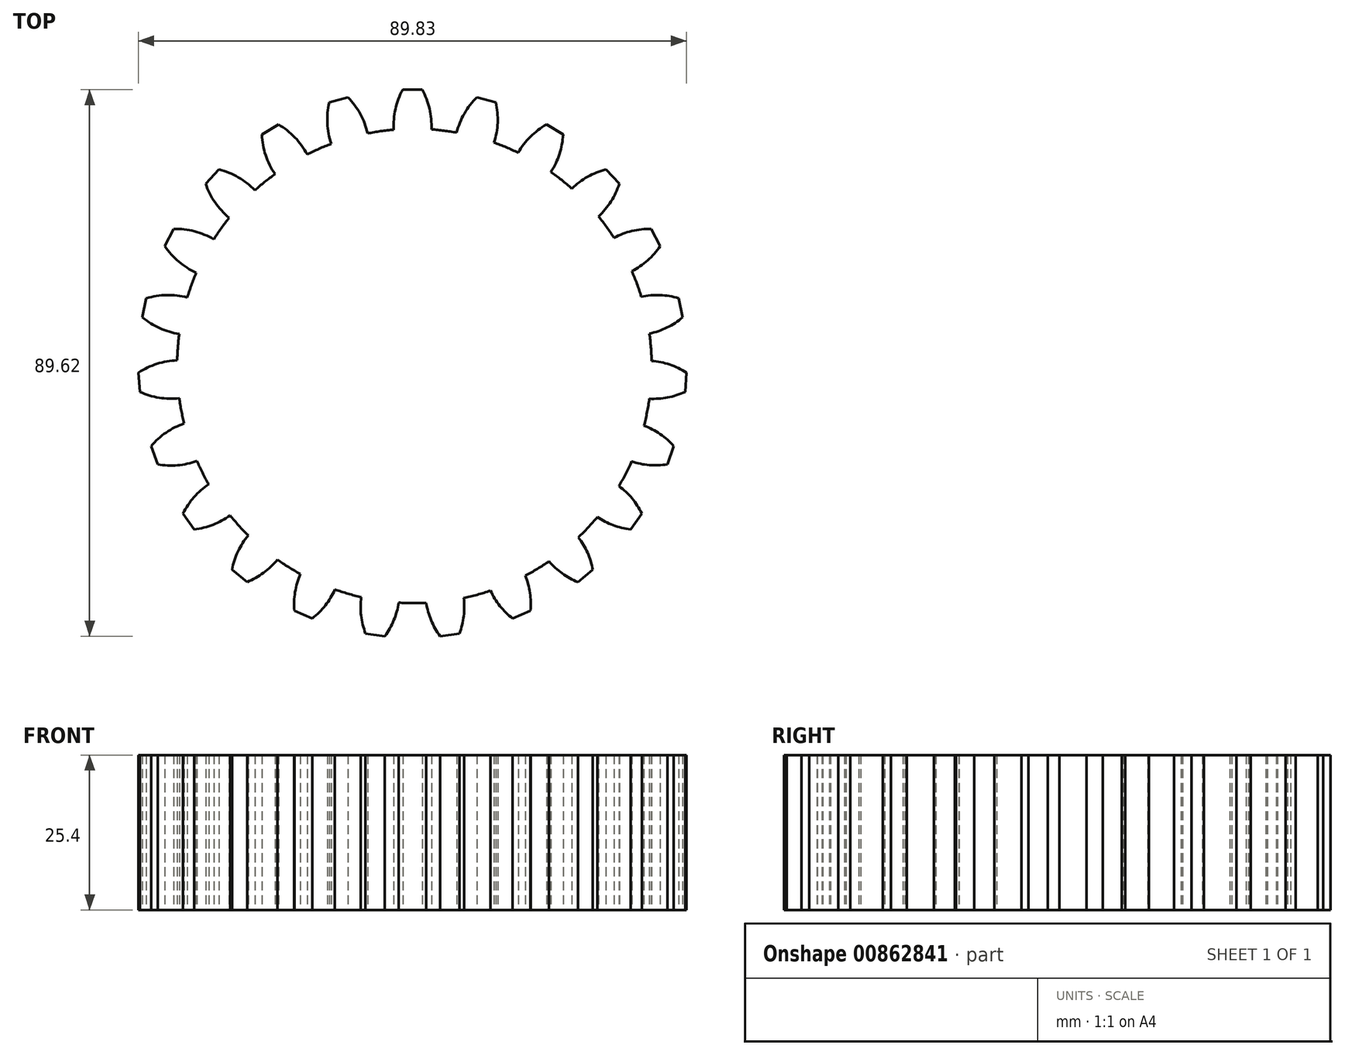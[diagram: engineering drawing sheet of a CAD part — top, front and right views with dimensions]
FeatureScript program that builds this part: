
annotation { "Feature Type Name" : "Feature", "Feature Type Description" : "" }
export const myFeature = defineFeature(function(context is Context, id is Id, definition is map)
    precondition{}
    {
        {
            var Q0;
            Q0=qCreatedBy(makeId("Top.planeOp"),FACE);
            var sketch = newSketch(context, id + "F0", { "sketchPlane" : qUnion([Q0])});
            skLineSegment(sketch, "E0.22.2", {"start": v(40.96, 115) * mm, "end": v(42.5, 115.43) * mm});
            skCircle(sketch, "E1", {"center": v(0, 0) * mm, "radius": 38.9 * mm});
            skArc(sketch, "E2", {"start": v(-1.9, 45.32) * mm, "mid": v(-3.1, 42.14) * mm, "end": v(-3.38, 38.75) * mm});
            skLineSegment(sketch, "E3", {"start": v(-1.9, 45.32) * mm, "end": v(-0.31, 45.32) * mm});
            skArc(sketch, "E4.MirrorCS", {"start": v(1.28, 45.32) * mm, "mid": v(2.49, 42.17) * mm, "end": v(2.8, 38.8) * mm});
            skLineSegment(sketch, "E5.MirrorCS", {"start": v(1.28, 45.32) * mm, "end": v(-0.31, 45.32) * mm});
            skArc(sketch, "E6.1.0", {"start": v(10.27, 44.08) * mm, "mid": v(8.2, 41.41) * mm, "end": v(6.92, 38.28) * mm});
            skArc(sketch, "E6.1.1", {"start": v(13.34, 43.23) * mm, "mid": v(13.65, 39.91) * mm, "end": v(13.07, 36.64) * mm});
            skLineSegment(sketch, "E6.1.2", {"start": v(10.27, 44.08) * mm, "end": v(11.8, 43.65) * mm});
            skLineSegment(sketch, "E6.1.3", {"start": v(13.34, 43.23) * mm, "end": v(11.8, 43.65) * mm});
            skArc(sketch, "E6.2.0", {"start": v(21.66, 39.6) * mm, "mid": v(19.03, 37.6) * mm, "end": v(17.02, 34.98) * mm});
            skArc(sketch, "E6.2.1", {"start": v(24.38, 37.96) * mm, "mid": v(23.79, 34.76) * mm, "end": v(22.37, 31.82) * mm});
            skLineSegment(sketch, "E6.2.2", {"start": v(21.66, 39.6) * mm, "end": v(23.02, 38.78) * mm});
            skLineSegment(sketch, "E6.2.3", {"start": v(24.38, 37.96) * mm, "end": v(23.02, 38.78) * mm});
            skArc(sketch, "E6.3.0", {"start": v(31.42, 32.23) * mm, "mid": v(28.41, 31.04) * mm, "end": v(25.81, 29.1) * mm});
            skArc(sketch, "E6.3.1", {"start": v(33.6, 29.9) * mm, "mid": v(32.25, 27) * mm, "end": v(30.2, 24.53) * mm});
            skLineSegment(sketch, "E6.3.2", {"start": v(31.42, 32.23) * mm, "end": v(32.5, 31.06) * mm});
            skLineSegment(sketch, "E6.3.3", {"start": v(33.6, 29.9) * mm, "end": v(32.5, 31.06) * mm});
            skArc(sketch, "E6.4.0", {"start": v(38.83, 22.48) * mm, "mid": v(35.67, 22.15) * mm, "end": v(32.7, 21.01) * mm});
            skArc(sketch, "E6.4.1", {"start": v(40.3, 19.66) * mm, "mid": v(38.2, 17.27) * mm, "end": v(35.56, 15.5) * mm});
            skLineSegment(sketch, "E6.4.2", {"start": v(38.83, 22.48) * mm, "end": v(39.56, 21.07) * mm});
            skLineSegment(sketch, "E6.4.3", {"start": v(40.3, 19.66) * mm, "end": v(39.56, 21.07) * mm});
            skArc(sketch, "E6.5.0", {"start": v(43.33, 11.1) * mm, "mid": v(40.2, 11.63) * mm, "end": v(37.04, 11.34) * mm});
            skArc(sketch, "E6.5.1", {"start": v(43.98, 7.99) * mm, "mid": v(41.32, 6.26) * mm, "end": v(38.3, 5.26) * mm});
            skLineSegment(sketch, "E6.5.2", {"start": v(43.33, 11.1) * mm, "end": v(43.66, 9.55) * mm});
            skLineSegment(sketch, "E6.5.3", {"start": v(43.98, 7.99) * mm, "end": v(43.66, 9.55) * mm});
            skArc(sketch, "E6.6.0", {"start": v(44.6, -1.07) * mm, "mid": v(41.73, 0.28) * mm, "end": v(38.6, 0.86) * mm});
            skArc(sketch, "E6.6.1", {"start": v(44.38, -4.24) * mm, "mid": v(41.35, -5.2) * mm, "end": v(38.18, -5.34) * mm});
            skLineSegment(sketch, "E6.6.2", {"start": v(44.6, -1.07) * mm, "end": v(44.5, -2.66) * mm});
            skLineSegment(sketch, "E6.6.3", {"start": v(44.38, -4.24) * mm, "end": v(44.5, -2.66) * mm});
            skArc(sketch, "E6.7.0", {"start": v(42.54, -13.13) * mm, "mid": v(40.13, -11.05) * mm, "end": v(37.28, -9.66) * mm});
            skArc(sketch, "E6.7.1", {"start": v(41.47, -16.13) * mm, "mid": v(38.3, -16.23) * mm, "end": v(35.2, -15.5) * mm});
            skLineSegment(sketch, "E6.7.2", {"start": v(42.54, -13.13) * mm, "end": v(42, -14.63) * mm});
            skLineSegment(sketch, "E6.7.3", {"start": v(41.47, -16.13) * mm, "end": v(42, -14.63) * mm});
            skArc(sketch, "E6.8.0", {"start": v(37.3, -24.19) * mm, "mid": v(35.54, -21.54) * mm, "end": v(33.17, -19.43) * mm});
            skArc(sketch, "E6.8.1", {"start": v(35.46, -26.8) * mm, "mid": v(32.38, -26.03) * mm, "end": v(29.59, -24.5) * mm});
            skLineSegment(sketch, "E6.8.2", {"start": v(37.3, -24.19) * mm, "end": v(36.38, -25.49) * mm});
            skLineSegment(sketch, "E6.8.3", {"start": v(35.46, -26.8) * mm, "end": v(36.38, -25.49) * mm});
            skArc(sketch, "E6.9.0", {"start": v(29.26, -33.42) * mm, "mid": v(28.29, -30.4) * mm, "end": v(26.58, -27.72) * mm});
            skArc(sketch, "E6.9.1", {"start": v(26.8, -35.43) * mm, "mid": v(24.03, -33.86) * mm, "end": v(21.76, -31.64) * mm});
            skLineSegment(sketch, "E6.9.2", {"start": v(29.26, -33.42) * mm, "end": v(28.03, -34.43) * mm});
            skLineSegment(sketch, "E6.9.3", {"start": v(26.8, -35.43) * mm, "end": v(28.03, -34.43) * mm});
            skArc(sketch, "E6.10.0", {"start": v(19.04, -40.15) * mm, "mid": v(18.92, -36.97) * mm, "end": v(17.99, -33.94) * mm});
            skArc(sketch, "E6.10.1", {"start": v(16.12, -41.42) * mm, "mid": v(13.88, -39.16) * mm, "end": v(12.3, -36.41) * mm});
            skLineSegment(sketch, "E6.10.2", {"start": v(19.04, -40.15) * mm, "end": v(17.58, -40.78) * mm});
            skLineSegment(sketch, "E6.10.3", {"start": v(16.12, -41.42) * mm, "end": v(17.58, -40.78) * mm});
            skArc(sketch, "E6.11.0", {"start": v(7.38, -43.87) * mm, "mid": v(8.12, -40.78) * mm, "end": v(8.04, -37.6) * mm});
            skArc(sketch, "E6.11.1", {"start": v(4.22, -44.3) * mm, "mid": v(2.68, -41.52) * mm, "end": v(1.9, -38.45) * mm});
            skLineSegment(sketch, "E6.11.2", {"start": v(7.38, -43.87) * mm, "end": v(5.8, -44.08) * mm});
            skLineSegment(sketch, "E6.11.3", {"start": v(4.22, -44.3) * mm, "end": v(5.8, -44.08) * mm});
            skArc(sketch, "E6.12.0", {"start": v(-4.85, -44.3) * mm, "mid": v(-3.3, -41.52) * mm, "end": v(-2.52, -38.45) * mm});
            skArc(sketch, "E6.12.1", {"start": v(-8, -43.87) * mm, "mid": v(-8.75, -40.78) * mm, "end": v(-8.67, -37.6) * mm});
            skLineSegment(sketch, "E6.12.2", {"start": v(-4.85, -44.3) * mm, "end": v(-6.43, -44.08) * mm});
            skLineSegment(sketch, "E6.12.3", {"start": v(-8, -43.87) * mm, "end": v(-6.43, -44.08) * mm});
            skArc(sketch, "E6.13.0", {"start": v(-16.75, -41.42) * mm, "mid": v(-14.51, -39.16) * mm, "end": v(-12.92, -36.41) * mm});
            skArc(sketch, "E6.13.1", {"start": v(-19.67, -40.15) * mm, "mid": v(-19.55, -36.97) * mm, "end": v(-18.62, -33.94) * mm});
            skLineSegment(sketch, "E6.13.2", {"start": v(-16.75, -41.42) * mm, "end": v(-18.2, -40.78) * mm});
            skLineSegment(sketch, "E6.13.3", {"start": v(-19.67, -40.15) * mm, "end": v(-18.2, -40.78) * mm});
            skArc(sketch, "E6.14.0", {"start": v(-27.42, -35.43) * mm, "mid": v(-24.66, -33.86) * mm, "end": v(-22.39, -31.64) * mm});
            skArc(sketch, "E6.14.1", {"start": v(-29.9, -33.42) * mm, "mid": v(-28.92, -30.4) * mm, "end": v(-27.2, -27.72) * mm});
            skLineSegment(sketch, "E6.14.2", {"start": v(-27.42, -35.43) * mm, "end": v(-28.66, -34.43) * mm});
            skLineSegment(sketch, "E6.14.3", {"start": v(-29.9, -33.42) * mm, "end": v(-28.66, -34.43) * mm});
            skArc(sketch, "E6.15.0", {"start": v(-36.09, -26.8) * mm, "mid": v(-33, -26.03) * mm, "end": v(-30.21, -24.5) * mm});
            skArc(sketch, "E6.15.1", {"start": v(-37.92, -24.19) * mm, "mid": v(-36.14, -21.52) * mm, "end": v(-33.72, -19.4) * mm});
            skLineSegment(sketch, "E6.15.2", {"start": v(-36.09, -26.8) * mm, "end": v(-37, -25.49) * mm});
            skLineSegment(sketch, "E6.15.3", {"start": v(-37.92, -24.19) * mm, "end": v(-37, -25.49) * mm});
            skArc(sketch, "E6.16.0", {"start": v(-42.1, -16.13) * mm, "mid": v(-38.84, -16.28) * mm, "end": v(-35.65, -15.58) * mm});
            skArc(sketch, "E6.16.1", {"start": v(-43.16, -13.13) * mm, "mid": v(-40.7, -10.9) * mm, "end": v(-37.74, -9.42) * mm});
            skLineSegment(sketch, "E6.16.2", {"start": v(-42.1, -16.13) * mm, "end": v(-42.63, -14.63) * mm});
            skLineSegment(sketch, "E6.16.3", {"start": v(-43.16, -13.13) * mm, "end": v(-42.63, -14.63) * mm});
            skArc(sketch, "E6.17.0", {"start": v(-45.01, -4.24) * mm, "mid": v(-41.85, -5.2) * mm, "end": v(-38.54, -5.29) * mm});
            skArc(sketch, "E6.17.1", {"start": v(-45.23, -1.07) * mm, "mid": v(-42.2, 0.36) * mm, "end": v(-38.89, 0.93) * mm});
            skLineSegment(sketch, "E6.17.2", {"start": v(-45.01, -4.24) * mm, "end": v(-45.12, -2.66) * mm});
            skLineSegment(sketch, "E6.17.3", {"start": v(-45.23, -1.07) * mm, "end": v(-45.12, -2.66) * mm});
            skArc(sketch, "E6.18.0", {"start": v(-44.6, 7.99) * mm, "mid": v(-41.77, 6.2) * mm, "end": v(-38.54, 5.25) * mm});
            skArc(sketch, "E6.18.1", {"start": v(-43.96, 11.1) * mm, "mid": v(-40.61, 11.64) * mm, "end": v(-37.24, 11.24) * mm});
            skLineSegment(sketch, "E6.18.2", {"start": v(-44.6, 7.99) * mm, "end": v(-44.29, 9.55) * mm});
            skLineSegment(sketch, "E6.18.3", {"start": v(-43.96, 11.1) * mm, "end": v(-44.29, 9.55) * mm});
            skArc(sketch, "E6.19.0", {"start": v(-40.92, 19.66) * mm, "mid": v(-38.64, 17.12) * mm, "end": v(-35.76, 15.3) * mm});
            skArc(sketch, "E6.19.1", {"start": v(-39.46, 22.48) * mm, "mid": v(-36.05, 22.1) * mm, "end": v(-32.89, 20.78) * mm});
            skLineSegment(sketch, "E6.19.2", {"start": v(-40.92, 19.66) * mm, "end": v(-40.19, 21.07) * mm});
            skLineSegment(sketch, "E6.19.3", {"start": v(-39.46, 22.48) * mm, "end": v(-40.19, 21.07) * mm});
            skArc(sketch, "E6.20.0", {"start": v(-34.22, 29.9) * mm, "mid": v(-32.7, 26.83) * mm, "end": v(-30.38, 24.3) * mm});
            skArc(sketch, "E6.20.1", {"start": v(-32.05, 32.23) * mm, "mid": v(-28.86, 30.93) * mm, "end": v(-26.15, 28.8) * mm});
            skLineSegment(sketch, "E6.20.2", {"start": v(-34.22, 29.9) * mm, "end": v(-33.14, 31.06) * mm});
            skLineSegment(sketch, "E6.20.3", {"start": v(-32.05, 32.23) * mm, "end": v(-33.14, 31.06) * mm});
            skArc(sketch, "E6.21.0", {"start": v(-25, 37.96) * mm, "mid": v(-24.39, 34.57) * mm, "end": v(-22.85, 31.48) * mm});
            skArc(sketch, "E6.21.1", {"start": v(-22.29, 39.6) * mm, "mid": v(-19.59, 37.49) * mm, "end": v(-17.58, 34.7) * mm});
            skLineSegment(sketch, "E6.21.2", {"start": v(-25, 37.96) * mm, "end": v(-23.65, 38.78) * mm});
            skLineSegment(sketch, "E6.21.3", {"start": v(-22.29, 39.6) * mm, "end": v(-23.65, 38.78) * mm});
            skArc(sketch, "E6.22.0", {"start": v(-13.96, 43.23) * mm, "mid": v(-14.27, 39.8) * mm, "end": v(-13.63, 36.44) * mm});
            skArc(sketch, "E6.22.1", {"start": v(-10.9, 44.08) * mm, "mid": v(-8.86, 41.34) * mm, "end": v(-7.66, 38.14) * mm});
            skLineSegment(sketch, "E6.22.2", {"start": v(-13.96, 43.23) * mm, "end": v(-12.43, 43.65) * mm});
            skLineSegment(sketch, "E6.22.3", {"start": v(-10.9, 44.08) * mm, "end": v(-12.43, 43.65) * mm});
            skArc(sketch, "E6.23.0", {"start": v(-1.9, 45.32) * mm, "mid": v(-3.06, 42.36) * mm, "end": v(-3.42, 39.2) * mm});
            skArc(sketch, "E6.23.1", {"start": v(1.28, 45.32) * mm, "mid": v(2.43, 42.36) * mm, "end": v(2.8, 39.2) * mm});
            skSolve(sketch);
        }
        {
            var Q0;
            Q0 = qSketchRegion(id + "F0", true);
            extrude(context, id + "F1", {"entities" : qUnion([Q0]), "depth" : 25.4 * mm, "offsetDistance" : 25.4 * mm});
        }
    });
